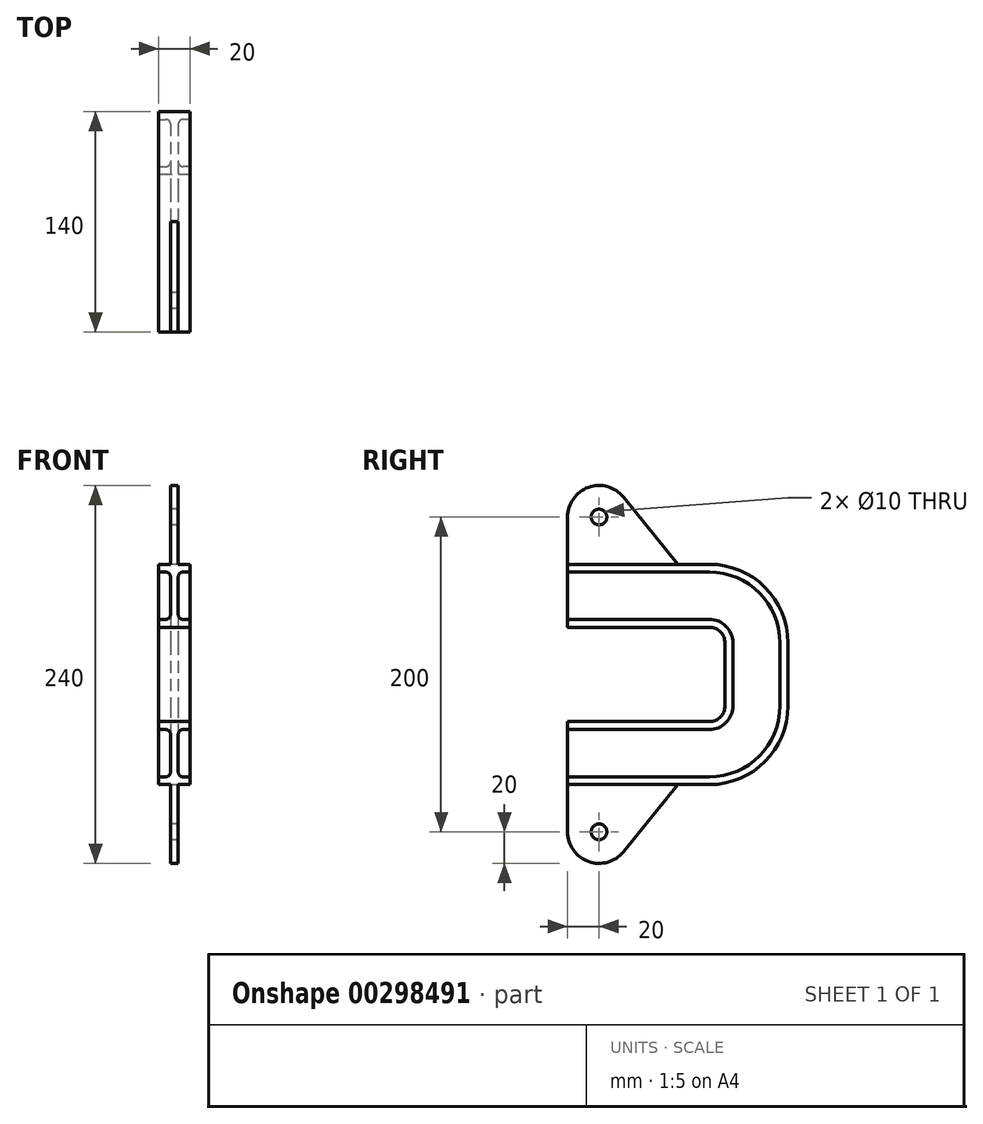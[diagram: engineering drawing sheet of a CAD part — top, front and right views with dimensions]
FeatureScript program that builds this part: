
annotation { "Feature Type Name" : "Feature", "Feature Type Description" : "" }
export const myFeature = defineFeature(function(context is Context, id is Id, definition is map)
    precondition{}
    {
        {
            var Q0;
            Q0=qCreatedBy(makeId("Front.planeOp"),FACE);
            var sketch = newSketch(context, id + "F0", { "sketchPlane" : qUnion([Q0])});
            skLineSegment(sketch, "E0", {"start": v(0, 20) * mm, "end": v(10, 20) * mm});
            skLineSegment(sketch, "E1", {"start": v(10, 20) * mm, "end": v(10, 15) * mm});
            skLineSegment(sketch, "E2", {"start": v(10, 15) * mm, "end": v(5.5, 15) * mm});
            skLineSegment(sketch, "E3", {"start": v(2.5, 12) * mm, "end": v(2.5, 0) * mm});
            skPoint(sketch, "E4.visualSharp", {"position": v(2.5, 15) * mm});
            skArc(sketch, "E4.filletArc", {"start": v(5.5, 15) * mm, "mid": v(3.38, 14.12) * mm, "end": v(2.5, 12) * mm});
            skArc(sketch, "E5.MirrorCS", {"start": v(-5.5, 15) * mm, "mid": v(-3.38, 14.12) * mm, "end": v(-2.5, 12) * mm});
            skLineSegment(sketch, "E6.MirrorCS", {"start": v(0, 20) * mm, "end": v(-10, 20) * mm});
            skLineSegment(sketch, "E7.MirrorCS", {"start": v(-10, 20) * mm, "end": v(-10, 15) * mm});
            skPoint(sketch, "E8.MirrorP", {"position": v(-2.5, 15) * mm});
            skLineSegment(sketch, "E9.MirrorCS", {"start": v(-10, 15) * mm, "end": v(-5.5, 15) * mm});
            skLineSegment(sketch, "E10.MirrorCS", {"start": v(-2.5, 12) * mm, "end": v(-2.5, 0) * mm});
            skArc(sketch, "E11.MirrorCS", {"start": v(5.5, -15) * mm, "mid": v(3.38, -14.12) * mm, "end": v(2.5, -12) * mm});
            skArc(sketch, "E12.MirrorCS", {"start": v(-5.5, -15) * mm, "mid": v(-3.38, -14.12) * mm, "end": v(-2.5, -12) * mm});
            skPoint(sketch, "E13.MirrorP", {"position": v(-2.5, -15) * mm});
            skLineSegment(sketch, "E14.MirrorCS", {"start": v(-2.5, -12) * mm, "end": v(-2.5, 0) * mm});
            skLineSegment(sketch, "E15.MirrorCS", {"start": v(-10, -15) * mm, "end": v(-5.5, -15) * mm});
            skLineSegment(sketch, "E16.MirrorCS", {"start": v(-10, -20) * mm, "end": v(-10, -15) * mm});
            skLineSegment(sketch, "E17.MirrorCS", {"start": v(0, -20) * mm, "end": v(-10, -20) * mm});
            skLineSegment(sketch, "E18.MirrorCS", {"start": v(10, -20) * mm, "end": v(10, -15) * mm});
            skLineSegment(sketch, "E19.MirrorCS", {"start": v(10, -15) * mm, "end": v(5.5, -15) * mm});
            skPoint(sketch, "E20.MirrorP", {"position": v(2.5, -15) * mm});
            skLineSegment(sketch, "E21.MirrorCS", {"start": v(0, -20) * mm, "end": v(10, -20) * mm});
            skLineSegment(sketch, "E22.MirrorCS", {"start": v(2.5, -12) * mm, "end": v(2.5, 0) * mm});
            skSolve(sketch);
        }
        {
            var Q0;
            Q0=qCreatedBy(makeId("Right.planeOp"),FACE);
            var sketch = newSketch(context, id + "F1", { "sketchPlane" : qUnion([Q0])});
            skLineSegment(sketch, "E23", {"start": v(0, -20) * mm, "end": v(90, -20) * mm});
            skLineSegment(sketch, "E24", {"start": v(100, -30) * mm, "end": v(100, -70) * mm});
            skLineSegment(sketch, "E25", {"start": v(90, -80) * mm, "end": v(0, -80) * mm});
            skPoint(sketch, "E26.visualSharp", {"position": v(100, -20) * mm});
            skArc(sketch, "E26.filletArc", {"start": v(100, -30) * mm, "mid": v(97.07, -22.93) * mm, "end": v(90, -20) * mm});
            skPoint(sketch, "E27.visualSharp", {"position": v(100, -80) * mm});
            skArc(sketch, "E27.filletArc", {"start": v(90, -80) * mm, "mid": v(97.07, -77.07) * mm, "end": v(100, -70) * mm});
            skSolve(sketch);
        }
        {
            var Q0;
            Q0 = qSketchRegion(id + "F0", true);
            var Q1;
            Q1 = qConstructionFilter(qBodyType(qCreatedBy(id + "F1" ,EDGE), BodyType.WIRE), ConstructionObject.NO);
            sweep(context, id + "F2", {"profiles" : qUnion([Q0]), "path" : qUnion([Q1])});
        }
        {
            var Q0;
            Q0=qCreatedBy(makeId("Right.planeOp"),FACE);
            var sketch = newSketch(context, id + "F3", { "sketchPlane" : qUnion([Q0])});
            skLineSegment(sketch, "E28", {"start": v(0, 20) * mm, "end": v(70, 20) * mm});
            skLineSegment(sketch, "E29", {"start": v(0, 20) * mm, "end": v(0, 50) * mm});
            skLineSegment(sketch, "E30", {"start": v(70, 20) * mm, "end": v(35.55, 62.58) * mm});
            skPoint(sketch, "E31.visualSharp", {"position": v(21.75, 74.92) * mm});
            skArc(sketch, "E31.filletArc", {"start": v(35.55, 62.58) * mm, "mid": v(13.33, 68.85) * mm, "end": v(0, 50) * mm});
            skCircle(sketch, "E32", {"center": v(20, 50) * mm, "radius": 5 * mm});
            skLineSegment(sketch, "E33", {"start": v(0, -120) * mm, "end": v(70, -120) * mm});
            skLineSegment(sketch, "E34", {"start": v(70, -120) * mm, "end": v(35.55, -162.58) * mm});
            skLineSegment(sketch, "E35", {"start": v(0, -150) * mm, "end": v(0, -120) * mm});
            skPoint(sketch, "E36.visualSharp", {"position": v(39.65, -159.23) * mm});
            skArc(sketch, "E36.filletArc", {"start": v(0, -150) * mm, "mid": v(13.33, -168.85) * mm, "end": v(35.55, -162.58) * mm});
            skCircle(sketch, "E37", {"center": v(20, -150) * mm, "radius": 5 * mm});
            skSolve(sketch);
        }
        {
            var Q0;
            Q0=makeQuery(id+"F3.imprint","IMPRINT",FACE,{"disambiguationData":[TD([[makeQuery(id+"F3.imprint","IMPRINT",EDGE,{"derivedFrom":sQuery(id+"F3.wireOp",EDGE,"E33")}),-1.0]])]});
            var Q1;
            Q1=makeQuery(id+"F3.imprint","IMPRINT",FACE,{"disambiguationData":[TD([[makeQuery(id+"F3.imprint","IMPRINT",EDGE,{"derivedFrom":sQuery(id+"F3.wireOp",EDGE,"E28")}),1.0]])]});
            extrude(context, id + "F4", {"entities" : qUnion([Q0, Q1]), "operationType" : NewBodyOperationType.ADD, "endBound" : BoundingType.SYMMETRIC, "depth" : 5 * mm});
        }
    });
